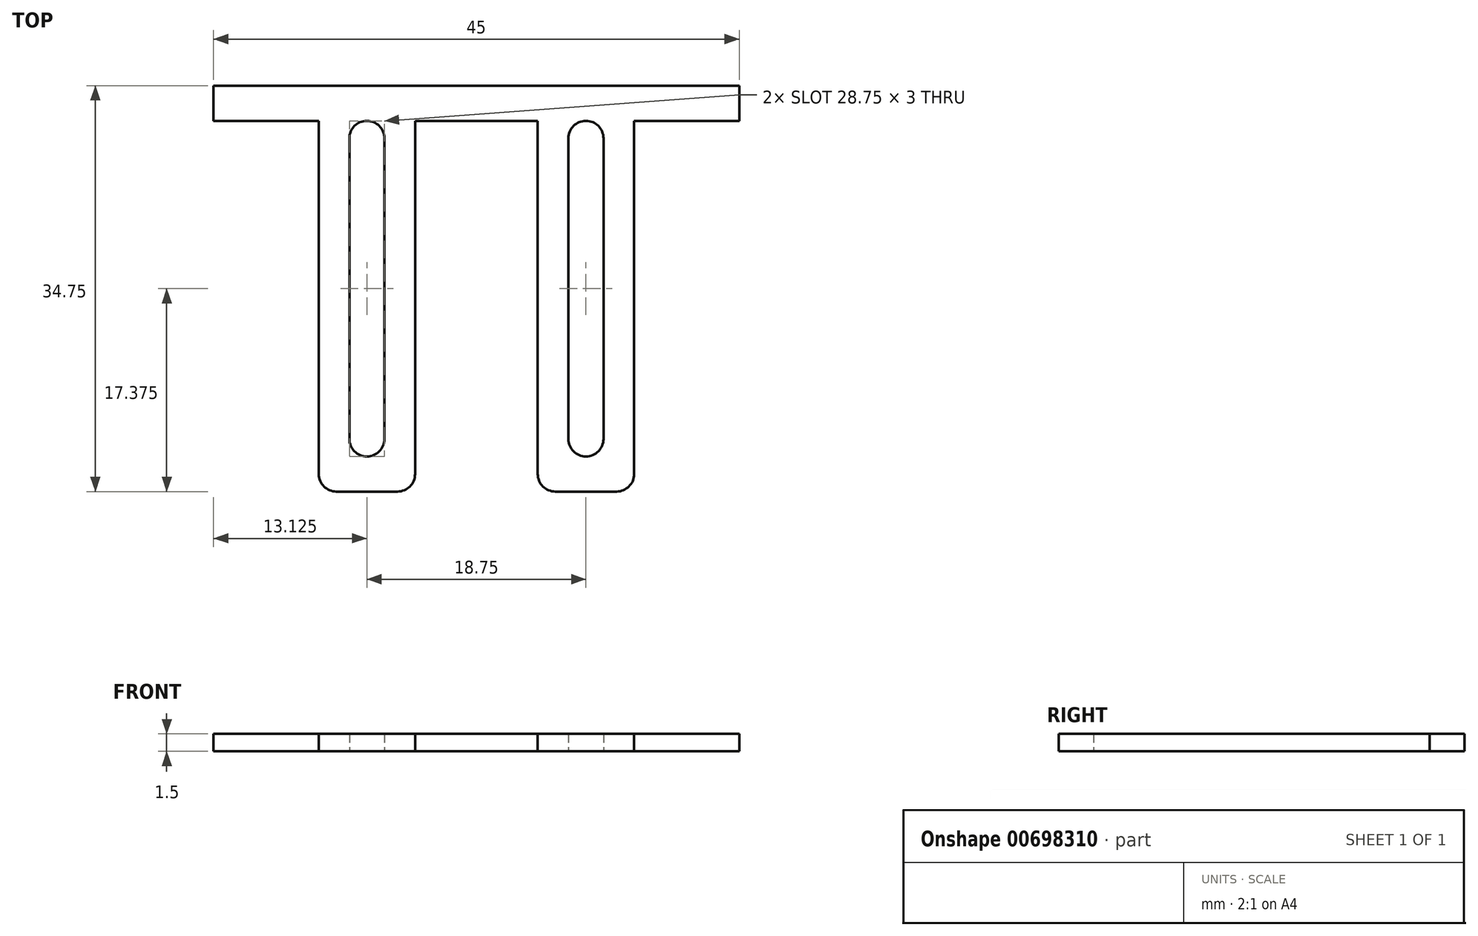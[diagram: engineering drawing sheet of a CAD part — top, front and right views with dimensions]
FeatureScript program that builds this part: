
annotation { "Feature Type Name" : "Feature", "Feature Type Description" : "" }
export const myFeature = defineFeature(function(context is Context, id is Id, definition is map)
    precondition{}
    {
        {
            var Q0;
            Q0=qCreatedBy(makeId("Top.planeOp"),FACE);
            var sketch = newSketch(context, id + "F0", { "sketchPlane" : qUnion([Q0])});
            skLineSegment(sketch, "E0", {"start": v(-22.5, 0) * mm, "end": v(22.5, 0) * mm});
            skLineSegment(sketch, "E1", {"start": v(22.5, 0) * mm, "end": v(22.5, -3) * mm});
            skLineSegment(sketch, "E2", {"start": v(22.5, -3) * mm, "end": v(13.5, -3) * mm});
            skLineSegment(sketch, "E3", {"start": v(13.5, -3) * mm, "end": v(13.5, -33.25) * mm});
            skLineSegment(sketch, "E4", {"start": v(12, -34.75) * mm, "end": v(6.75, -34.75) * mm});
            skLineSegment(sketch, "E5", {"start": v(5.25, -33.25) * mm, "end": v(5.25, -3) * mm});
            skLineSegment(sketch, "E6", {"start": v(5.25, -3) * mm, "end": v(-5.25, -3) * mm});
            skLineSegment(sketch, "E7", {"start": v(-5.25, -3) * mm, "end": v(-5.25, -33.25) * mm});
            skLineSegment(sketch, "E8", {"start": v(-6.75, -34.75) * mm, "end": v(-12, -34.75) * mm});
            skLineSegment(sketch, "E9", {"start": v(-13.5, -33.25) * mm, "end": v(-13.5, -3) * mm});
            skLineSegment(sketch, "E10", {"start": v(-13.5, -3) * mm, "end": v(-22.5, -3) * mm});
            skLineSegment(sketch, "E11", {"start": v(-22.5, -3) * mm, "end": v(-22.5, 0) * mm});
            skArc(sketch, "E12", {"start": v(-13.5, -33.25) * mm, "mid": v(-13.06, -34.31) * mm, "end": v(-12, -34.75) * mm});
            skArc(sketch, "E13", {"start": v(-6.75, -34.75) * mm, "mid": v(-5.69, -34.31) * mm, "end": v(-5.25, -33.25) * mm});
            skArc(sketch, "E14", {"start": v(5.25, -33.25) * mm, "mid": v(5.69, -34.31) * mm, "end": v(6.75, -34.75) * mm});
            skArc(sketch, "E15", {"start": v(12, -34.75) * mm, "mid": v(13.06, -34.31) * mm, "end": v(13.5, -33.25) * mm});
            skPoint(sketch, "E16.orphan", {"position": v(-5.25, -34.75) * mm});
            skPoint(sketch, "E17.orphan", {"position": v(13.5, -34.75) * mm});
            skArc(sketch, "E18", {"start": v(-7.88, -4.5) * mm, "mid": v(-9.38, -3) * mm, "end": v(-10.88, -4.5) * mm});
            skArc(sketch, "E19", {"start": v(10.88, -4.5) * mm, "mid": v(9.38, -3) * mm, "end": v(7.88, -4.5) * mm});
            skArc(sketch, "E20", {"start": v(7.88, -30.25) * mm, "mid": v(9.38, -31.75) * mm, "end": v(10.88, -30.25) * mm});
            skArc(sketch, "E21", {"start": v(-10.88, -30.25) * mm, "mid": v(-9.38, -31.75) * mm, "end": v(-7.88, -30.25) * mm});
            skLineSegment(sketch, "E22", {"start": v(-10.88, -4.5) * mm, "end": v(-10.87, -30.25) * mm});
            skLineSegment(sketch, "E23", {"start": v(-7.87, -30.25) * mm, "end": v(-7.88, -4.5) * mm});
            skLineSegment(sketch, "E24", {"start": v(7.88, -4.5) * mm, "end": v(7.88, -30.25) * mm});
            skLineSegment(sketch, "E25", {"start": v(10.88, -4.5) * mm, "end": v(10.88, -30.25) * mm});
            skSolve(sketch);
        }
        {
            var Q0;
            Q0 = qSketchRegion(id + "F0", true);
            extrude(context, id + "F1", {"entities" : qUnion([Q0]), "depth" : 1.5 * mm, "offsetDistance" : 25 * mm});
        }
    });
